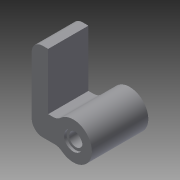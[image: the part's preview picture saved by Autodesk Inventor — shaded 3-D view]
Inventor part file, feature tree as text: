
AUTODESK INVENTOR PART (.ipt)
format: ipt  version: 2015 (Build 190159000, 159)  size: 131,584 bytes
history: native  units: in
note: dims shown in document units (in); Inventor stores cm internally (conversion verified against a paired STEP export)
features: extrude x4, sketch x4, mirror x1, fillet x1, reference x1
ambient origin geometry x8: Origin, YZ Plane, XZ Plane, XY Plane, X Axis, Y Axis, Z Axis, Center Point
bodies: Solid1 (feature_tree)
feature tree (11):
  extrude  "Extrusion1"  Depth=0.9375in TaperAngle=0.0deg
  extrude  "Extrusion2"  Depth=0.4882in TaperAngle=0.0deg
  mirror  "Mirror1"
  extrude  "Extrusion3"  Depth=0.0591in TaperAngle=0.0deg
  extrude  "Extrusion4"  Depth=1.8455in
  fillet  "Fillet1"  Radius=0.531in
  sketch  "Sketch1"  dims[d0=0.375in d1=0.0in d2=0.9375in d3=0.0in]
  reference  "Reference1"
  sketch  "Sketch2"  dims[d4=0.3125in d5=0.4882in d6=0.0in]
  sketch  "Sketch3"  dims[d7=0.4331in d8=0.0591in d9=0.0in]
  sketch  "Sketch4"  dims[d10=0.25in d11=1.8455in d12=0.531in]
